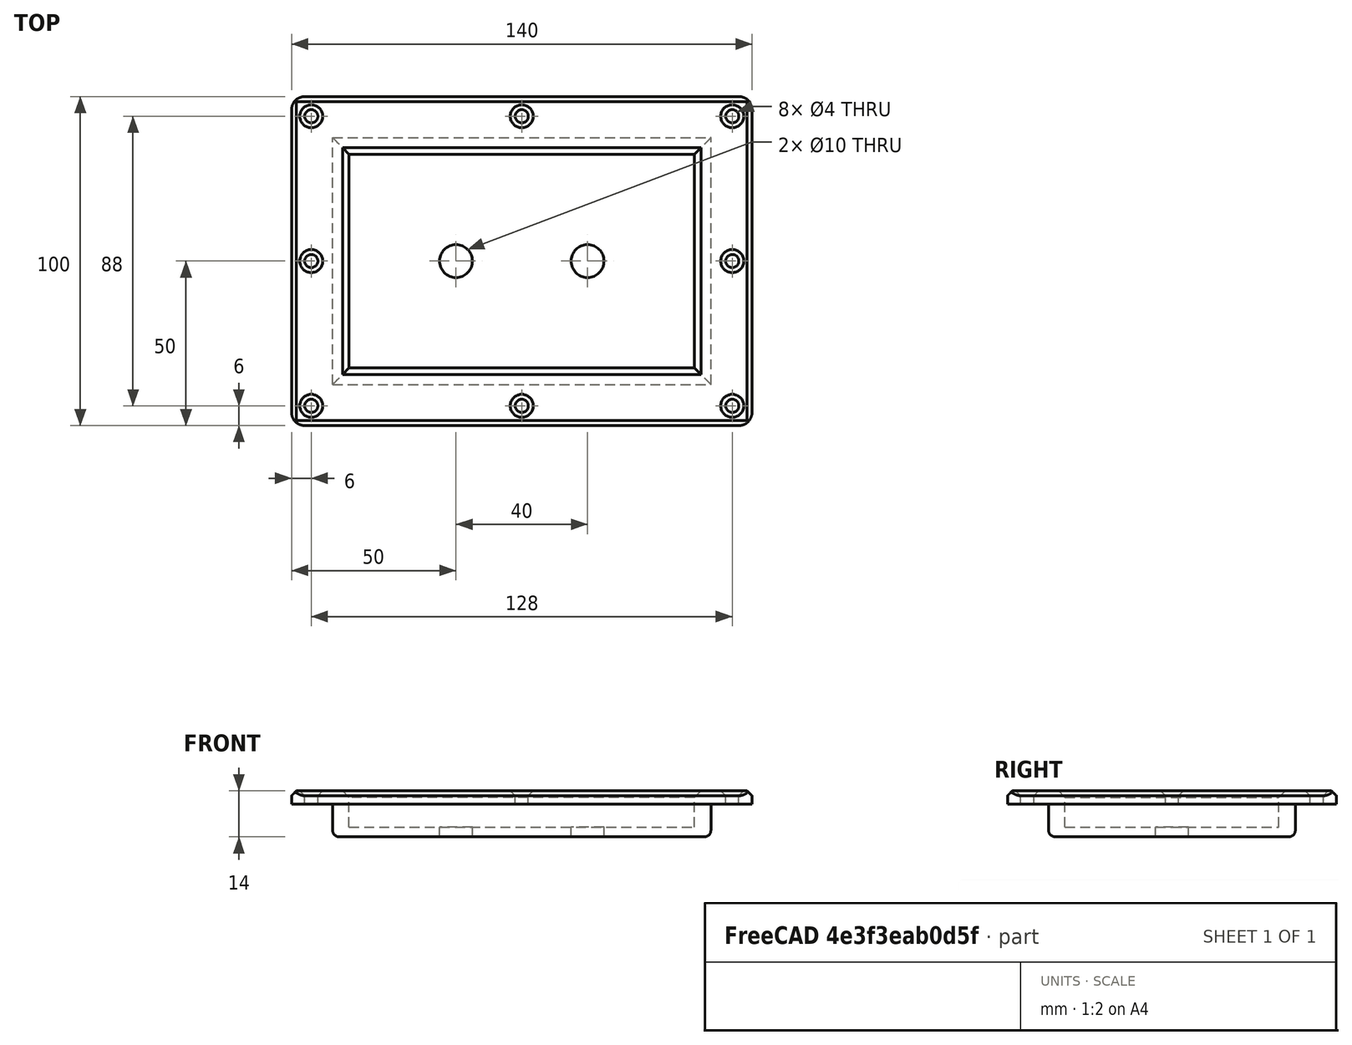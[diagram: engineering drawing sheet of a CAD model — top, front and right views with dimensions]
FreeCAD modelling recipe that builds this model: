
FCSTD DOCUMENT  (FreeCAD 0.15R4671 (Git))
Label: floor-monitor-plate-double
License: All rights reserved
LicenseURL: http://en.wikipedia.org/wiki/All_rights_reserved
objects: Part::Cut×11, Part::Cylinder×10, Part::Box×3, Part::Fillet×3, PartDesign::Chamfer×2, Part::Fuse×1, Part::Chamfer×1, Drawing::FeatureViewPart×1, Drawing::FeaturePage×1
note: 31 computed .brp shape members not serialized (recipe doc carries the construction recipe); baked Part::Feature solids carry a one-line shape summary decoded from their .brp

FEATURE [Part::Box] Box  label="Cube"
  Height = 4
  Length = 140
  Width = 100
FEATURE [Part::Cylinder] Cylinder
  Angle = 360
  Height = 10
  Placement = pos=(134,6,0) rot=(0,0,1;0rad)
  Radius = 2
FEATURE [Part::Cylinder] Cylinder001
  Angle = 360
  Height = 10
  Placement = pos=(134,50,0) rot=(0,0,1;0rad)
  Radius = 2
FEATURE [Part::Cylinder] Cylinder002
  Angle = 360
  Height = 10
  Placement = pos=(6,50,0) rot=(0,0,1;0rad)
  Radius = 2
FEATURE [Part::Cylinder] Cylinder003
  Angle = 360
  Height = 10
  Placement = pos=(6,94,0) rot=(0,0,1;0rad)
  Radius = 2
FEATURE [Part::Cylinder] Cylinder004
  Angle = 360
  Height = 10
  Placement = pos=(6,6,0) rot=(0,0,1;0rad)
  Radius = 2
FEATURE [Part::Cylinder] Cylinder005
  Angle = 360
  Height = 10
  Placement = pos=(134,94,0) rot=(0,0,1;0rad)
  Radius = 2
FEATURE [Part::Cut] Cut
  Base = -> Box
  Tool = -> Cylinder
FEATURE [Part::Cut] Cut001
  Base = -> Cut
  Tool = -> Cylinder001
FEATURE [Part::Cut] Cut002
  Base = -> Cut001
  Tool = -> Cylinder005
FEATURE [Part::Cut] Cut003
  Base = -> Cut002
  Tool = -> Cylinder004
FEATURE [Part::Cut] Cut004
  Base = -> Cut003
  Tool = -> Cylinder002
FEATURE [Part::Cut] Cut005
  Base = -> Cut004
  Placement = pos=(0,0,10) rot=(0,0,1;0rad)
  Tool = -> Cylinder003
FEATURE [PartDesign::Chamfer] Chamfer
  Base = -> Cut005 [Edge11,Edge14,Edge2,Edge8,Edge7,Edge9,Edge10,Edge12,Edge13,Edge15]
  Placement = pos=(0,0,10) rot=(0,0,1;0rad)
  Size = 1.5
FEATURE [Part::Cylinder] Cylinder006
  Angle = 360
  Height = 20
  Placement = pos=(50,50,-5) rot=(0,0,1;0rad)
  Radius = 5
FEATURE [Part::Box] Box001  label="Cube001"
  Height = 10
  Length = 115
  Placement = pos=(12.5,12.5,0) rot=(0,0,1;0rad)
  Width = 75
FEATURE [Part::Fillet] Fillet
  Base = -> Box001
  Edges = 4 edges r=2: [Edge4,Edge8,Edge9,Edge11]
FEATURE [Part::Box] Box002  label="Cube002"
  Height = 20
  Length = 105
  Placement = pos=(17.5,17.5,3) rot=(0,0,1;0rad)
  Width = 65
FEATURE [Part::Fuse] Fusion
  Base = -> Chamfer
  Tool = -> Fillet
FEATURE [Part::Cut] Cut006
  Base = -> Fusion
  Tool = -> Box002
FEATURE [Part::Cut] Cut007
  Base = -> Cut006
  Tool = -> Cylinder006
FEATURE [PartDesign::Chamfer] Chamfer001
  Base = -> Cut007 [Edge30,Edge33,Edge32,Edge31]
  Size = 2
FEATURE [Part::Fillet] Fillet001
  Base = -> Chamfer001
  Edges = 2 edges r=4: [Edge54,Edge56]
FEATURE [Part::Fillet] Fillet002
  Base = -> Fillet001
  Edges = 2 edges r=4: [Edge7,Edge31]
FEATURE [Part::Cylinder] Cylinder007
  Angle = 360
  Height = 20
  Placement = pos=(70,94,0) rot=(0,0,1;0rad)
  Radius = 2
FEATURE [Part::Cut] Cut008
  Base = -> Fillet002
  Tool = -> Cylinder007
FEATURE [Part::Cylinder] Cylinder008
  Angle = 360
  Height = 20
  Placement = pos=(70,6,0) rot=(0,0,1;0rad)
  Radius = 2
FEATURE [Part::Cut] Cut009
  Base = -> Cut008
  Tool = -> Cylinder008
FEATURE [Part::Chamfer] Chamfer002
  Base = -> Cut009
  Edges = 2 edges r=1.5: [Edge27,Edge29]
FEATURE [Drawing::FeatureViewPart] View001
  Direction = (0,0,1)
  HiddenWidth = 0.15
  LineWidth = 0.35
  Rotation = 0
  ShowHiddenLines = false
  ShowSmoothLines = false
  Source = -> Chamfer002
  Tolerance = 0.05
  ViewResult = <blob: 4398 chars omitted>
  Visible = true
  X = 50
  Y = 130
FEATURE [Drawing::FeaturePage] Page
  EditableTexts = Designed by Name | Date | Scale | Weight | Title | Subtitle | Drawing number | Sheet
  Group = -> [View001]
  Template = D:/Program Files/FreeCAD 0.15/data/Mod/Drawing/Templates/A4_Landscape.svg
FEATURE [Part::Cylinder] Cylinder009
  Angle = 360
  Height = 20
  Placement = pos=(90,50,-5) rot=(0,0,1;0rad)
  Radius = 5
FEATURE [Part::Cut] Cut010
  Base = -> Chamfer002
  Tool = -> Cylinder009
